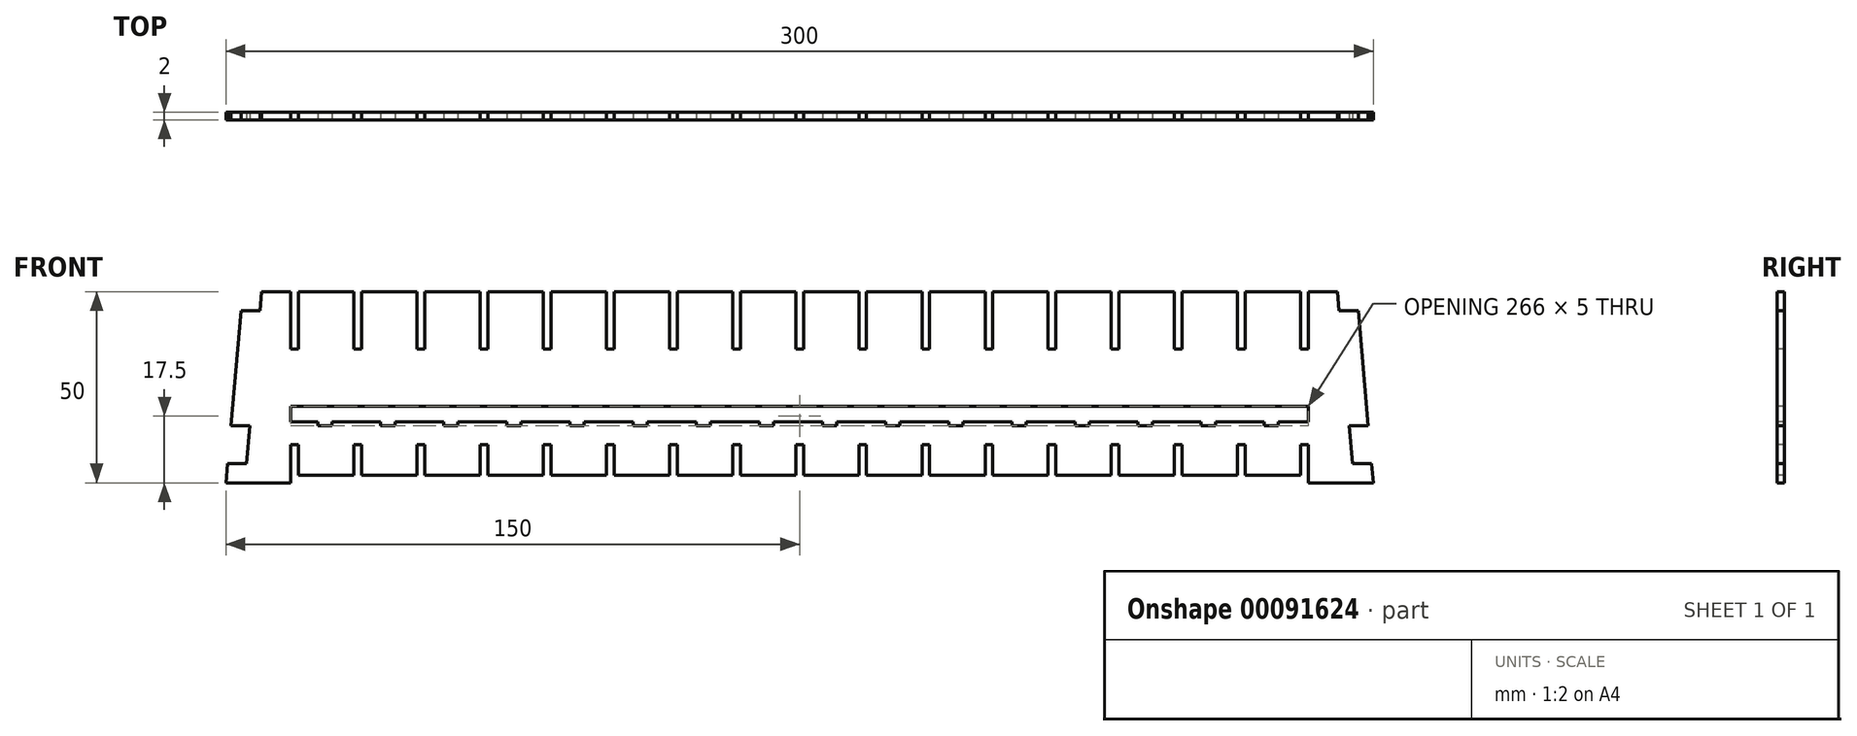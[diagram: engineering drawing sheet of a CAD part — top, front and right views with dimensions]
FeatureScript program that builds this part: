
annotation { "Feature Type Name" : "Feature", "Feature Type Description" : "" }
export const myFeature = defineFeature(function(context is Context, id is Id, definition is map)
    precondition{}
    {
        {
            var Q0;
            Q0=qCreatedBy(makeId("Front.planeOp"),FACE);
            var sketch = newSketch(context, id + "F0", { "sketchPlane" : qUnion([Q0])});
            skLineSegment(sketch, "E0", {"start": v(0, 0) * mm, "end": v(3.94, 45) * mm});
            skLineSegment(sketch, "E1", {"start": v(17, 50) * mm, "end": v(17, 35) * mm});
            skLineSegment(sketch, "E2", {"start": v(17, 35) * mm, "end": v(19, 35) * mm});
            skLineSegment(sketch, "E3", {"start": v(19, 35) * mm, "end": v(19, 50) * mm});
            skLineSegment(sketch, "E4", {"start": v(19, 50) * mm, "end": v(33.5, 50) * mm});
            skLineSegment(sketch, "E5", {"start": v(17, 0) * mm, "end": v(0, 0) * mm});
            skLineSegment(sketch, "E6", {"start": v(33.5, 50) * mm, "end": v(33.5, 35) * mm});
            skLineSegment(sketch, "E7", {"start": v(33.5, 35) * mm, "end": v(35.5, 35) * mm});
            skLineSegment(sketch, "E8", {"start": v(35.5, 35) * mm, "end": v(35.5, 50) * mm});
            skLineSegment(sketch, "E9", {"start": v(35.5, 50) * mm, "end": v(50, 50) * mm});
            skLineSegment(sketch, "E10", {"start": v(50, 50) * mm, "end": v(50, 35) * mm});
            skLineSegment(sketch, "E11", {"start": v(50, 35) * mm, "end": v(52, 35) * mm});
            skLineSegment(sketch, "E12", {"start": v(52, 35) * mm, "end": v(52, 50) * mm});
            skLineSegment(sketch, "E13", {"start": v(52, 50) * mm, "end": v(66.5, 50) * mm});
            skLineSegment(sketch, "E14", {"start": v(66.5, 50) * mm, "end": v(66.5, 35) * mm});
            skLineSegment(sketch, "E15", {"start": v(66.5, 35) * mm, "end": v(68.5, 35) * mm});
            skLineSegment(sketch, "E16", {"start": v(68.5, 35) * mm, "end": v(68.5, 50) * mm});
            skLineSegment(sketch, "E17", {"start": v(68.5, 50) * mm, "end": v(83, 50) * mm});
            skLineSegment(sketch, "E18", {"start": v(83, 50) * mm, "end": v(83, 35) * mm});
            skLineSegment(sketch, "E19", {"start": v(83, 35) * mm, "end": v(85, 35) * mm});
            skLineSegment(sketch, "E20", {"start": v(85, 35) * mm, "end": v(85, 50) * mm});
            skLineSegment(sketch, "E21", {"start": v(85, 50) * mm, "end": v(99.5, 50) * mm});
            skLineSegment(sketch, "E22", {"start": v(99.5, 50) * mm, "end": v(99.5, 35) * mm});
            skLineSegment(sketch, "E23", {"start": v(99.5, 35) * mm, "end": v(101.5, 35) * mm});
            skLineSegment(sketch, "E24", {"start": v(101.5, 35) * mm, "end": v(101.5, 50) * mm});
            skLineSegment(sketch, "E25", {"start": v(101.5, 50) * mm, "end": v(116, 50) * mm});
            skLineSegment(sketch, "E26", {"start": v(116, 50) * mm, "end": v(116, 35) * mm});
            skLineSegment(sketch, "E27", {"start": v(116, 35) * mm, "end": v(118, 35) * mm});
            skLineSegment(sketch, "E28", {"start": v(118, 35) * mm, "end": v(118, 50) * mm});
            skLineSegment(sketch, "E29", {"start": v(118, 50) * mm, "end": v(132.5, 50) * mm});
            skLineSegment(sketch, "E30", {"start": v(132.5, 50) * mm, "end": v(132.5, 35) * mm});
            skLineSegment(sketch, "E31", {"start": v(132.5, 35) * mm, "end": v(134.5, 35) * mm});
            skLineSegment(sketch, "E32", {"start": v(134.5, 35) * mm, "end": v(134.5, 50) * mm});
            skLineSegment(sketch, "E33", {"start": v(134.5, 50) * mm, "end": v(149, 50) * mm});
            skLineSegment(sketch, "E34", {"start": v(149, 50) * mm, "end": v(149, 35) * mm});
            skLineSegment(sketch, "E35", {"start": v(149, 35) * mm, "end": v(151, 35) * mm});
            skLineSegment(sketch, "E36", {"start": v(151, 35) * mm, "end": v(151, 50) * mm});
            skLineSegment(sketch, "E37", {"start": v(151, 50) * mm, "end": v(165.5, 50) * mm});
            skLineSegment(sketch, "E38", {"start": v(165.5, 50) * mm, "end": v(165.5, 35) * mm});
            skLineSegment(sketch, "E39", {"start": v(165.5, 35) * mm, "end": v(167.5, 35) * mm});
            skLineSegment(sketch, "E40", {"start": v(167.5, 35) * mm, "end": v(167.5, 50) * mm});
            skLineSegment(sketch, "E41", {"start": v(167.5, 50) * mm, "end": v(182, 50) * mm});
            skLineSegment(sketch, "E42", {"start": v(182, 50) * mm, "end": v(182, 35) * mm});
            skLineSegment(sketch, "E43", {"start": v(182, 35) * mm, "end": v(184, 35) * mm});
            skLineSegment(sketch, "E44", {"start": v(184, 35) * mm, "end": v(184, 50) * mm});
            skLineSegment(sketch, "E45", {"start": v(184, 50) * mm, "end": v(198.5, 50) * mm});
            skLineSegment(sketch, "E46", {"start": v(198.5, 50) * mm, "end": v(198.5, 35) * mm});
            skLineSegment(sketch, "E47", {"start": v(198.5, 35) * mm, "end": v(200.5, 35) * mm});
            skLineSegment(sketch, "E48", {"start": v(200.5, 35) * mm, "end": v(200.5, 50) * mm});
            skLineSegment(sketch, "E49", {"start": v(200.5, 50) * mm, "end": v(215, 50) * mm});
            skLineSegment(sketch, "E50", {"start": v(215, 50) * mm, "end": v(215, 35) * mm});
            skLineSegment(sketch, "E51", {"start": v(215, 35) * mm, "end": v(217, 35) * mm});
            skLineSegment(sketch, "E52", {"start": v(217, 35) * mm, "end": v(217, 50) * mm});
            skLineSegment(sketch, "E53", {"start": v(217, 50) * mm, "end": v(231.5, 50) * mm});
            skLineSegment(sketch, "E54", {"start": v(231.5, 50) * mm, "end": v(231.5, 35) * mm});
            skLineSegment(sketch, "E55", {"start": v(231.5, 35) * mm, "end": v(233.5, 35) * mm});
            skLineSegment(sketch, "E56", {"start": v(233.5, 35) * mm, "end": v(233.5, 50) * mm});
            skLineSegment(sketch, "E57", {"start": v(233.5, 50) * mm, "end": v(248, 50) * mm});
            skLineSegment(sketch, "E58", {"start": v(248, 50) * mm, "end": v(248, 35) * mm});
            skLineSegment(sketch, "E59", {"start": v(248, 35) * mm, "end": v(250, 35) * mm});
            skLineSegment(sketch, "E60", {"start": v(250, 35) * mm, "end": v(250, 50) * mm});
            skLineSegment(sketch, "E61", {"start": v(250, 50) * mm, "end": v(264.5, 50) * mm});
            skLineSegment(sketch, "E62", {"start": v(264.5, 50) * mm, "end": v(264.5, 35) * mm});
            skLineSegment(sketch, "E63", {"start": v(264.5, 35) * mm, "end": v(266.5, 35) * mm});
            skLineSegment(sketch, "E64", {"start": v(266.5, 35) * mm, "end": v(266.5, 50) * mm});
            skLineSegment(sketch, "E65", {"start": v(300, 0) * mm, "end": v(283, 0) * mm});
            skLineSegment(sketch, "E66", {"start": v(283, 10) * mm, "end": v(281, 10) * mm});
            skLineSegment(sketch, "E67", {"start": v(281, 2) * mm, "end": v(266.5, 2) * mm});
            skLineSegment(sketch, "E68", {"start": v(266.5, 10) * mm, "end": v(264.5, 10) * mm});
            skLineSegment(sketch, "E69", {"start": v(264.5, 2) * mm, "end": v(250, 2) * mm});
            skLineSegment(sketch, "E70", {"start": v(250, 10) * mm, "end": v(248, 10) * mm});
            skLineSegment(sketch, "E71", {"start": v(248, 2) * mm, "end": v(233.5, 2) * mm});
            skLineSegment(sketch, "E72", {"start": v(233.5, 10) * mm, "end": v(231.5, 10) * mm});
            skLineSegment(sketch, "E73", {"start": v(231.5, 2) * mm, "end": v(217, 2) * mm});
            skLineSegment(sketch, "E74", {"start": v(217, 10) * mm, "end": v(215, 10) * mm});
            skLineSegment(sketch, "E75", {"start": v(215, 2) * mm, "end": v(200.5, 2) * mm});
            skLineSegment(sketch, "E76", {"start": v(200.5, 10) * mm, "end": v(198.5, 10) * mm});
            skLineSegment(sketch, "E77", {"start": v(198.5, 2) * mm, "end": v(184, 2) * mm});
            skLineSegment(sketch, "E78", {"start": v(184, 10) * mm, "end": v(182, 10) * mm});
            skLineSegment(sketch, "E79", {"start": v(182, 2) * mm, "end": v(167.5, 2) * mm});
            skLineSegment(sketch, "E80", {"start": v(167.5, 10) * mm, "end": v(165.5, 10) * mm});
            skLineSegment(sketch, "E81", {"start": v(165.5, 2) * mm, "end": v(151, 2) * mm});
            skLineSegment(sketch, "E82", {"start": v(151, 10) * mm, "end": v(149, 10) * mm});
            skLineSegment(sketch, "E83", {"start": v(149, 2) * mm, "end": v(134.5, 2) * mm});
            skLineSegment(sketch, "E84", {"start": v(134.5, 10) * mm, "end": v(132.5, 10) * mm});
            skLineSegment(sketch, "E85", {"start": v(132.5, 2) * mm, "end": v(118, 2) * mm});
            skLineSegment(sketch, "E86", {"start": v(118, 10) * mm, "end": v(116, 10) * mm});
            skLineSegment(sketch, "E87", {"start": v(116, 2) * mm, "end": v(101.5, 2) * mm});
            skLineSegment(sketch, "E88", {"start": v(101.5, 10) * mm, "end": v(99.5, 10) * mm});
            skLineSegment(sketch, "E89", {"start": v(99.5, 2) * mm, "end": v(85, 2) * mm});
            skLineSegment(sketch, "E90", {"start": v(85, 10) * mm, "end": v(83, 10) * mm});
            skLineSegment(sketch, "E91", {"start": v(83, 2) * mm, "end": v(68.5, 2) * mm});
            skLineSegment(sketch, "E92", {"start": v(68.5, 10) * mm, "end": v(66.5, 10) * mm});
            skLineSegment(sketch, "E93", {"start": v(66.5, 2) * mm, "end": v(52, 2) * mm});
            skLineSegment(sketch, "E94", {"start": v(52, 10) * mm, "end": v(50, 10) * mm});
            skLineSegment(sketch, "E95", {"start": v(50, 2) * mm, "end": v(35.5, 2) * mm});
            skLineSegment(sketch, "E96", {"start": v(19, 10) * mm, "end": v(17, 10) * mm});
            skLineSegment(sketch, "E97", {"start": v(19, 10) * mm, "end": v(19, 2) * mm});
            skLineSegment(sketch, "E98", {"start": v(19, 2) * mm, "end": v(33.5, 2) * mm});
            skLineSegment(sketch, "E99", {"start": v(33.5, 2) * mm, "end": v(33.5, 10) * mm});
            skLineSegment(sketch, "E100", {"start": v(33.5, 10) * mm, "end": v(35.5, 10) * mm});
            skLineSegment(sketch, "E101", {"start": v(35.5, 10) * mm, "end": v(35.5, 2) * mm});
            skLineSegment(sketch, "E102", {"start": v(266.5, 50) * mm, "end": v(281, 50) * mm});
            skLineSegment(sketch, "E103", {"start": v(281, 50) * mm, "end": v(281, 35) * mm});
            skLineSegment(sketch, "E104", {"start": v(281, 35) * mm, "end": v(283, 35) * mm});
            skLineSegment(sketch, "E105", {"start": v(283, 35) * mm, "end": v(283, 50) * mm});
            skLineSegment(sketch, "E106", {"start": v(283, 50) * mm, "end": v(290.63, 50) * mm});
            skLineSegment(sketch, "E107", {"start": v(296.06, 45) * mm, "end": v(291.06, 45) * mm});
            skLineSegment(sketch, "E108", {"start": v(291.06, 45) * mm, "end": v(290.63, 50) * mm});
            skLineSegment(sketch, "E109", {"start": v(296.06, 45) * mm, "end": v(300, 0) * mm});
            skLineSegment(sketch, "E110", {"start": v(9.37, 50) * mm, "end": v(8.94, 45) * mm});
            skLineSegment(sketch, "E111", {"start": v(8.94, 45) * mm, "end": v(3.94, 45) * mm});
            skLineSegment(sketch, "E112", {"start": v(9.37, 50) * mm, "end": v(17, 50) * mm});
            skLineSegment(sketch, "E113", {"start": v(17, 0) * mm, "end": v(17, 10) * mm});
            skLineSegment(sketch, "E114", {"start": v(50, 2) * mm, "end": v(50, 10) * mm});
            skLineSegment(sketch, "E115", {"start": v(52, 2) * mm, "end": v(52, 10) * mm});
            skLineSegment(sketch, "E116", {"start": v(66.5, 2) * mm, "end": v(66.5, 10) * mm});
            skLineSegment(sketch, "E117", {"start": v(68.5, 2) * mm, "end": v(68.5, 10) * mm});
            skLineSegment(sketch, "E118", {"start": v(83, 2) * mm, "end": v(83, 10) * mm});
            skLineSegment(sketch, "E119", {"start": v(85, 2) * mm, "end": v(85, 10) * mm});
            skLineSegment(sketch, "E120", {"start": v(99.5, 2) * mm, "end": v(99.5, 10) * mm});
            skLineSegment(sketch, "E121", {"start": v(101.5, 2) * mm, "end": v(101.5, 10) * mm});
            skLineSegment(sketch, "E122", {"start": v(116, 2) * mm, "end": v(116, 10) * mm});
            skLineSegment(sketch, "E123", {"start": v(118, 2) * mm, "end": v(118, 10) * mm});
            skLineSegment(sketch, "E124", {"start": v(132.5, 2) * mm, "end": v(132.5, 10) * mm});
            skLineSegment(sketch, "E125", {"start": v(134.5, 2) * mm, "end": v(134.5, 10) * mm});
            skLineSegment(sketch, "E126", {"start": v(149, 2) * mm, "end": v(149, 10) * mm});
            skLineSegment(sketch, "E127", {"start": v(151, 2) * mm, "end": v(151, 10) * mm});
            skLineSegment(sketch, "E128", {"start": v(165.5, 2) * mm, "end": v(165.5, 10) * mm});
            skLineSegment(sketch, "E129", {"start": v(167.5, 2) * mm, "end": v(167.5, 10) * mm});
            skLineSegment(sketch, "E130", {"start": v(182, 2) * mm, "end": v(182, 10) * mm});
            skLineSegment(sketch, "E131", {"start": v(184, 2) * mm, "end": v(184, 10) * mm});
            skLineSegment(sketch, "E132", {"start": v(198.5, 2) * mm, "end": v(198.5, 10) * mm});
            skLineSegment(sketch, "E133", {"start": v(200.5, 2) * mm, "end": v(200.5, 10) * mm});
            skLineSegment(sketch, "E134", {"start": v(215, 2) * mm, "end": v(215, 10) * mm});
            skLineSegment(sketch, "E135", {"start": v(217, 2) * mm, "end": v(217, 10) * mm});
            skLineSegment(sketch, "E136", {"start": v(231.5, 2) * mm, "end": v(231.5, 10) * mm});
            skLineSegment(sketch, "E137", {"start": v(233.5, 2) * mm, "end": v(233.5, 10) * mm});
            skLineSegment(sketch, "E138", {"start": v(248, 2) * mm, "end": v(248, 10) * mm});
            skLineSegment(sketch, "E139", {"start": v(250, 2) * mm, "end": v(250, 10) * mm});
            skLineSegment(sketch, "E140", {"start": v(264.5, 2) * mm, "end": v(264.5, 10) * mm});
            skLineSegment(sketch, "E141", {"start": v(266.5, 2) * mm, "end": v(266.5, 10) * mm});
            skLineSegment(sketch, "E142", {"start": v(281, 2) * mm, "end": v(281, 10) * mm});
            skLineSegment(sketch, "E143", {"start": v(283, 0) * mm, "end": v(283, 10) * mm});
            skSolve(sketch);
        }
        {
            var Q0;
            Q0=makeQuery(id+"F0.imprint","IMPRINT",FACE,{"disambiguationData":[TD([[makeQuery(id+"F0.imprint","IMPRINT",EDGE,{"derivedFrom":sQuery(id+"F0.wireOp",EDGE,"E0")}),-1.0]])]});
            extrude(context, id + "F1", {"entities" : qUnion([Q0]), "oppositeDirection" : true, "depth" : 2 * mm});
        }
        {
            var Q0;
            Q0=qCreatedBy(makeId("Front.planeOp"),FACE);
            var sketch = newSketch(context, id + "F2", { "sketchPlane" : qUnion([Q0])});
            skLineSegment(sketch, "E144", {"start": v(17, 20) * mm, "end": v(283, 20) * mm});
            skLineSegment(sketch, "E145", {"start": v(283, 20) * mm, "end": v(283, 16) * mm});
            skLineSegment(sketch, "E146", {"start": v(17, 20) * mm, "end": v(17, 16) * mm});
            skLineSegment(sketch, "E147", {"start": v(17, 16) * mm, "end": v(24, 16) * mm});
            skLineSegment(sketch, "E148", {"start": v(24, 16) * mm, "end": v(24, 15) * mm});
            skLineSegment(sketch, "E149", {"start": v(24, 15) * mm, "end": v(27.7, 15) * mm});
            skLineSegment(sketch, "E150", {"start": v(27.7, 15) * mm, "end": v(27.7, 16) * mm});
            skLineSegment(sketch, "E151", {"start": v(27.7, 16) * mm, "end": v(40.5, 16) * mm});
            skLineSegment(sketch, "E152", {"start": v(40.5, 16) * mm, "end": v(40.5, 15) * mm});
            skLineSegment(sketch, "E153", {"start": v(40.5, 15) * mm, "end": v(44.2, 15) * mm});
            skLineSegment(sketch, "E154", {"start": v(44.2, 15) * mm, "end": v(44.2, 16) * mm});
            skLineSegment(sketch, "E155", {"start": v(44.2, 16) * mm, "end": v(57, 16) * mm});
            skLineSegment(sketch, "E156", {"start": v(57, 16) * mm, "end": v(57, 15) * mm});
            skLineSegment(sketch, "E157", {"start": v(57, 15) * mm, "end": v(60.7, 15) * mm});
            skLineSegment(sketch, "E158", {"start": v(60.7, 15) * mm, "end": v(60.7, 16) * mm});
            skLineSegment(sketch, "E159", {"start": v(60.7, 16) * mm, "end": v(73.5, 16) * mm});
            skLineSegment(sketch, "E160", {"start": v(73.5, 16) * mm, "end": v(73.5, 15) * mm});
            skLineSegment(sketch, "E161", {"start": v(93.7, 16) * mm, "end": v(93.7, 15) * mm});
            skLineSegment(sketch, "E162", {"start": v(93.7, 15) * mm, "end": v(90, 15) * mm});
            skLineSegment(sketch, "E163", {"start": v(90, 15) * mm, "end": v(90, 16) * mm});
            skLineSegment(sketch, "E164", {"start": v(106.5, 16) * mm, "end": v(106.5, 15) * mm});
            skLineSegment(sketch, "E165", {"start": v(106.5, 15) * mm, "end": v(110.2, 15) * mm});
            skLineSegment(sketch, "E166", {"start": v(110.2, 15) * mm, "end": v(110.2, 16) * mm});
            skLineSegment(sketch, "E167", {"start": v(110.2, 16) * mm, "end": v(123, 16) * mm});
            skLineSegment(sketch, "E168", {"start": v(123, 16) * mm, "end": v(123, 15) * mm});
            skLineSegment(sketch, "E169", {"start": v(123, 15) * mm, "end": v(126.7, 15) * mm});
            skLineSegment(sketch, "E170", {"start": v(126.7, 15) * mm, "end": v(126.7, 16) * mm});
            skLineSegment(sketch, "E171", {"start": v(126.7, 16) * mm, "end": v(139.5, 16) * mm});
            skLineSegment(sketch, "E172", {"start": v(139.5, 16) * mm, "end": v(139.5, 15) * mm});
            skLineSegment(sketch, "E173", {"start": v(139.5, 15) * mm, "end": v(143.2, 15) * mm});
            skLineSegment(sketch, "E174", {"start": v(143.2, 15) * mm, "end": v(143.2, 16) * mm});
            skLineSegment(sketch, "E175", {"start": v(143.2, 16) * mm, "end": v(156, 16) * mm});
            skLineSegment(sketch, "E176", {"start": v(156, 16) * mm, "end": v(156, 15) * mm});
            skLineSegment(sketch, "E177", {"start": v(156, 15) * mm, "end": v(159.7, 15) * mm});
            skLineSegment(sketch, "E178", {"start": v(159.7, 15) * mm, "end": v(159.7, 16) * mm});
            skLineSegment(sketch, "E179", {"start": v(159.7, 16) * mm, "end": v(172.5, 16) * mm});
            skLineSegment(sketch, "E180", {"start": v(172.5, 16) * mm, "end": v(172.5, 15) * mm});
            skLineSegment(sketch, "E181", {"start": v(172.5, 15) * mm, "end": v(176.2, 15) * mm});
            skLineSegment(sketch, "E182", {"start": v(176.2, 15) * mm, "end": v(176.2, 16) * mm});
            skLineSegment(sketch, "E183", {"start": v(238.5, 16) * mm, "end": v(238.5, 15) * mm});
            skLineSegment(sketch, "E184", {"start": v(238.5, 15) * mm, "end": v(242.2, 15) * mm});
            skLineSegment(sketch, "E185", {"start": v(242.2, 15) * mm, "end": v(242.2, 16) * mm});
            skLineSegment(sketch, "E186", {"start": v(242.2, 16) * mm, "end": v(255, 16) * mm});
            skLineSegment(sketch, "E187", {"start": v(255, 16) * mm, "end": v(255, 15) * mm});
            skLineSegment(sketch, "E188", {"start": v(255, 15) * mm, "end": v(258.7, 15) * mm});
            skLineSegment(sketch, "E189", {"start": v(258.7, 15) * mm, "end": v(258.7, 16) * mm});
            skLineSegment(sketch, "E190", {"start": v(258.7, 16) * mm, "end": v(271.5, 16) * mm});
            skLineSegment(sketch, "E191", {"start": v(271.5, 16) * mm, "end": v(271.5, 15) * mm});
            skLineSegment(sketch, "E192", {"start": v(271.5, 15) * mm, "end": v(275.2, 15) * mm});
            skLineSegment(sketch, "E193", {"start": v(275.2, 15) * mm, "end": v(275.2, 16) * mm});
            skLineSegment(sketch, "E194", {"start": v(189, 16) * mm, "end": v(189, 15) * mm});
            skLineSegment(sketch, "E195", {"start": v(189, 15) * mm, "end": v(192.7, 15) * mm});
            skLineSegment(sketch, "E196", {"start": v(192.7, 15) * mm, "end": v(192.7, 16) * mm});
            skLineSegment(sketch, "E197", {"start": v(192.7, 16) * mm, "end": v(205.5, 16) * mm});
            skLineSegment(sketch, "E198", {"start": v(205.5, 16) * mm, "end": v(205.5, 15) * mm});
            skLineSegment(sketch, "E199", {"start": v(205.5, 15) * mm, "end": v(209.2, 15) * mm});
            skLineSegment(sketch, "E200", {"start": v(209.2, 15) * mm, "end": v(209.2, 16) * mm});
            skLineSegment(sketch, "E201", {"start": v(209.2, 16) * mm, "end": v(222, 16) * mm});
            skLineSegment(sketch, "E202", {"start": v(222, 16) * mm, "end": v(222, 15) * mm});
            skLineSegment(sketch, "E203", {"start": v(222, 15) * mm, "end": v(225.7, 15) * mm});
            skLineSegment(sketch, "E204", {"start": v(225.7, 15) * mm, "end": v(225.7, 16) * mm});
            skLineSegment(sketch, "E205", {"start": v(73.5, 15) * mm, "end": v(77.2, 15) * mm});
            skLineSegment(sketch, "E206", {"start": v(77.2, 15) * mm, "end": v(77.2, 16) * mm});
            skLineSegment(sketch, "E207", {"start": v(77.2, 16) * mm, "end": v(90, 16) * mm});
            skLineSegment(sketch, "E208", {"start": v(93.7, 16) * mm, "end": v(106.5, 16) * mm});
            skLineSegment(sketch, "E209", {"start": v(176.2, 16) * mm, "end": v(189, 16) * mm});
            skLineSegment(sketch, "E210", {"start": v(225.7, 16) * mm, "end": v(238.5, 16) * mm});
            skLineSegment(sketch, "E211", {"start": v(275.2, 16) * mm, "end": v(283, 16) * mm});
            skLineSegment(sketch, "E212", {"start": v(0.44, 5) * mm, "end": v(5.44, 5) * mm});
            skLineSegment(sketch, "E213", {"start": v(5.44, 5) * mm, "end": v(6.31, 15) * mm});
            skLineSegment(sketch, "E214", {"start": v(6.31, 15) * mm, "end": v(1.31, 15) * mm});
            skLineSegment(sketch, "E215", {"start": v(1.31, 15) * mm, "end": v(0.44, 5) * mm});
            skLineSegment(sketch, "E216", {"start": v(293.69, 15) * mm, "end": v(294.56, 5) * mm});
            skLineSegment(sketch, "E217", {"start": v(294.56, 5) * mm, "end": v(299.56, 5) * mm});
            skLineSegment(sketch, "E218", {"start": v(299.56, 5) * mm, "end": v(298.69, 15) * mm});
            skLineSegment(sketch, "E219", {"start": v(298.69, 15) * mm, "end": v(293.69, 15) * mm});
            skSolve(sketch);
        }
        {
            var Q0;
            Q0 = qSketchRegion(id + "F2", true);
            var Q1;
            Q1=makeQuery(id+"F1.opExtrude","CAP_FACE",FACE,{"disambiguationData":[OSD([sQuery(id+"F0.wireOp",EDGE,"E0"),sQuery(id+"F0.wireOp",EDGE,"HgcZy7nT-3lwv-bNy9-udKW-1yyANhBGPKqc"),sQuery(id+"F0.wireOp",EDGE,"E1"),sQuery(id+"F0.wireOp",EDGE,"E2"),sQuery(id+"F0.wireOp",EDGE,"E3"),sQuery(id+"F0.wireOp",EDGE,"E4"),sQuery(id+"F0.wireOp",EDGE,"E5"),sQuery(id+"F0.wireOp",EDGE,"E6"),sQuery(id+"F0.wireOp",EDGE,"E7"),sQuery(id+"F0.wireOp",EDGE,"E8"),sQuery(id+"F0.wireOp",EDGE,"E9"),sQuery(id+"F0.wireOp",EDGE,"E10"),sQuery(id+"F0.wireOp",EDGE,"E11"),sQuery(id+"F0.wireOp",EDGE,"E12"),sQuery(id+"F0.wireOp",EDGE,"E13"),sQuery(id+"F0.wireOp",EDGE,"E14"),sQuery(id+"F0.wireOp",EDGE,"E15"),sQuery(id+"F0.wireOp",EDGE,"E16"),sQuery(id+"F0.wireOp",EDGE,"E17"),sQuery(id+"F0.wireOp",EDGE,"E18"),sQuery(id+"F0.wireOp",EDGE,"E19"),sQuery(id+"F0.wireOp",EDGE,"E20"),sQuery(id+"F0.wireOp",EDGE,"E21"),sQuery(id+"F0.wireOp",EDGE,"E22"),sQuery(id+"F0.wireOp",EDGE,"E23"),sQuery(id+"F0.wireOp",EDGE,"E24"),sQuery(id+"F0.wireOp",EDGE,"E25"),sQuery(id+"F0.wireOp",EDGE,"E26"),sQuery(id+"F0.wireOp",EDGE,"E27"),sQuery(id+"F0.wireOp",EDGE,"E28"),sQuery(id+"F0.wireOp",EDGE,"E29"),sQuery(id+"F0.wireOp",EDGE,"E30"),sQuery(id+"F0.wireOp",EDGE,"E31"),sQuery(id+"F0.wireOp",EDGE,"E32"),sQuery(id+"F0.wireOp",EDGE,"E33"),sQuery(id+"F0.wireOp",EDGE,"E34"),sQuery(id+"F0.wireOp",EDGE,"E35"),sQuery(id+"F0.wireOp",EDGE,"E36"),sQuery(id+"F0.wireOp",EDGE,"E37"),sQuery(id+"F0.wireOp",EDGE,"E38"),sQuery(id+"F0.wireOp",EDGE,"E39"),sQuery(id+"F0.wireOp",EDGE,"E40"),sQuery(id+"F0.wireOp",EDGE,"E41"),sQuery(id+"F0.wireOp",EDGE,"E42"),sQuery(id+"F0.wireOp",EDGE,"E43"),sQuery(id+"F0.wireOp",EDGE,"E44"),sQuery(id+"F0.wireOp",EDGE,"E45"),sQuery(id+"F0.wireOp",EDGE,"E46"),sQuery(id+"F0.wireOp",EDGE,"E47"),sQuery(id+"F0.wireOp",EDGE,"E48"),sQuery(id+"F0.wireOp",EDGE,"E49"),sQuery(id+"F0.wireOp",EDGE,"E50"),sQuery(id+"F0.wireOp",EDGE,"E51"),sQuery(id+"F0.wireOp",EDGE,"E52"),sQuery(id+"F0.wireOp",EDGE,"E53"),sQuery(id+"F0.wireOp",EDGE,"E54"),sQuery(id+"F0.wireOp",EDGE,"E55"),sQuery(id+"F0.wireOp",EDGE,"E56"),sQuery(id+"F0.wireOp",EDGE,"E57"),sQuery(id+"F0.wireOp",EDGE,"E58"),sQuery(id+"F0.wireOp",EDGE,"E59"),sQuery(id+"F0.wireOp",EDGE,"E60"),sQuery(id+"F0.wireOp",EDGE,"E61"),sQuery(id+"F0.wireOp",EDGE,"E62"),sQuery(id+"F0.wireOp",EDGE,"E63"),sQuery(id+"F0.wireOp",EDGE,"E64"),sQuery(id+"F0.wireOp",EDGE,"BVOWMFHa-wpLm-4TX3-Hbss-mqhhteEW6FXH"),sQuery(id+"F0.wireOp",EDGE,"E65"),sQuery(id+"F0.wireOp",EDGE,"Ny0LBNpl-DC1b-g7gX-uDmU-KXUJp1Uvs8bH"),sQuery(id+"F0.wireOp",EDGE,"E66"),sQuery(id+"F0.wireOp",EDGE,"L0EVueSU-Bzzz-ozeF-6hyl-cjv2B7mdk9nX"),sQuery(id+"F0.wireOp",EDGE,"E67"),sQuery(id+"F0.wireOp",EDGE,"z7V8Xtq7-9ljz-YrJZ-rfjC-Y5BD1rRiIm1u"),sQuery(id+"F0.wireOp",EDGE,"E68"),sQuery(id+"F0.wireOp",EDGE,"YCztE2ad-vpCO-r5Er-xRay-cPCHDfHWENhY"),sQuery(id+"F0.wireOp",EDGE,"E69"),sQuery(id+"F0.wireOp",EDGE,"hall3pES-sXyJ-vu0Y-LRwG-adX0xoJdBjPT"),sQuery(id+"F0.wireOp",EDGE,"E70"),sQuery(id+"F0.wireOp",EDGE,"HapMSiuU-j1My-omjA-AIKl-s35L9K1DCdMv"),sQuery(id+"F0.wireOp",EDGE,"E71"),sQuery(id+"F0.wireOp",EDGE,"cxGI27vh-PhuA-DEnV-wgYv-RIFEEykBdlIG"),sQuery(id+"F0.wireOp",EDGE,"E72"),sQuery(id+"F0.wireOp",EDGE,"4pOcXCnN-Qqmk-RNP6-p9ZY-k7VT3SrKYYIm"),sQuery(id+"F0.wireOp",EDGE,"E73"),sQuery(id+"F0.wireOp",EDGE,"IvOV3hIr-bj6g-dsOc-59va-o6hrhdawShYW"),sQuery(id+"F0.wireOp",EDGE,"E74"),sQuery(id+"F0.wireOp",EDGE,"aiYAQkSz-ye5B-NAvN-EaHV-yYgKXb2guKy2"),sQuery(id+"F0.wireOp",EDGE,"E75"),sQuery(id+"F0.wireOp",EDGE,"deSUF8Wy-izGZ-KJL7-F7sa-vv7DJSF65tzd"),sQuery(id+"F0.wireOp",EDGE,"E76"),sQuery(id+"F0.wireOp",EDGE,"knURT3mm-qJ5e-uAEv-XtMx-gx8QacUYlODw"),sQuery(id+"F0.wireOp",EDGE,"E77"),sQuery(id+"F0.wireOp",EDGE,"JvS8wIF9-GTxq-Shxd-HEk2-VQDqqqWf2vDR"),sQuery(id+"F0.wireOp",EDGE,"E78"),sQuery(id+"F0.wireOp",EDGE,"hC3mFLkM-rNt6-YxLP-T6Ut-VB35484fw7rg"),sQuery(id+"F0.wireOp",EDGE,"E79"),sQuery(id+"F0.wireOp",EDGE,"03HSr1IS-cMoz-EuO1-jhf5-BLUVcBS5aCII"),sQuery(id+"F0.wireOp",EDGE,"E80"),sQuery(id+"F0.wireOp",EDGE,"4pRiP4Qb-GxdF-G7ua-kPKT-rGo3PBmFVMMh"),sQuery(id+"F0.wireOp",EDGE,"E81"),sQuery(id+"F0.wireOp",EDGE,"31KDk3w8-zvsP-PMm4-8rSG-4di7emiA55pW"),sQuery(id+"F0.wireOp",EDGE,"E82"),sQuery(id+"F0.wireOp",EDGE,"8IrskNiL-fo41-gDwx-3q5M-fVGG1YOBFxI9"),sQuery(id+"F0.wireOp",EDGE,"E83"),sQuery(id+"F0.wireOp",EDGE,"CSi5XsMw-pvjV-rWde-ON5c-3UqJn2YIq8jn"),sQuery(id+"F0.wireOp",EDGE,"E84"),sQuery(id+"F0.wireOp",EDGE,"MBxpImWm-eRvk-aWU8-U4yn-nKg3TTCsLjfT"),sQuery(id+"F0.wireOp",EDGE,"E85"),sQuery(id+"F0.wireOp",EDGE,"FSR2KC9K-EGrI-nhKE-Fi6A-T41pzSywKCEg"),sQuery(id+"F0.wireOp",EDGE,"E86"),sQuery(id+"F0.wireOp",EDGE,"I2Vx5CsF-7VTe-yqni-W39r-mekiYP3QSefZ"),sQuery(id+"F0.wireOp",EDGE,"E87"),sQuery(id+"F0.wireOp",EDGE,"0cDBUIyj-6oQs-NqVM-rf7f-aOtaGS2aotWP"),sQuery(id+"F0.wireOp",EDGE,"E88"),sQuery(id+"F0.wireOp",EDGE,"yMGYaIAU-y6q6-IKF7-ToxC-SvuajWYre8og"),sQuery(id+"F0.wireOp",EDGE,"E89"),sQuery(id+"F0.wireOp",EDGE,"ZftYtxsV-UZJY-z8ZW-g9Gq-ohFEgne7n6v0"),sQuery(id+"F0.wireOp",EDGE,"E90"),sQuery(id+"F0.wireOp",EDGE,"vxcZILMP-886a-ghS7-RbWO-ZaSI4S1PIg1K"),sQuery(id+"F0.wireOp",EDGE,"E91"),sQuery(id+"F0.wireOp",EDGE,"IlgRW5Ga-Fsin-zCQm-a4KG-mxPj2x5quiJ4"),sQuery(id+"F0.wireOp",EDGE,"E92"),sQuery(id+"F0.wireOp",EDGE,"zQP4WX22-XsxW-SWvl-jWig-XTAqm5llDSmK"),sQuery(id+"F0.wireOp",EDGE,"E93"),sQuery(id+"F0.wireOp",EDGE,"OQ0uxrJ9-YOf8-i4xL-ogb8-zCvbwl5xDN57"),sQuery(id+"F0.wireOp",EDGE,"E94"),sQuery(id+"F0.wireOp",EDGE,"JCZAKs25-YOuf-8OKZ-4fvG-gDuP2TVhTKYT"),sQuery(id+"F0.wireOp",EDGE,"E95"),sQuery(id+"F0.wireOp",EDGE,"E96"),sQuery(id+"F0.wireOp",EDGE,"P1PESZwT-Sg2v-Tdse-M8t0-1K99oKy4DD9l"),sQuery(id+"F0.wireOp",EDGE,"E97"),sQuery(id+"F0.wireOp",EDGE,"E98"),sQuery(id+"F0.wireOp",EDGE,"E99"),sQuery(id+"F0.wireOp",EDGE,"E100"),sQuery(id+"F0.wireOp",EDGE,"E101"),sQuery(id+"F0.wireOp",EDGE,"E102"),sQuery(id+"F0.wireOp",EDGE,"E103"),sQuery(id+"F0.wireOp",EDGE,"E104"),sQuery(id+"F0.wireOp",EDGE,"E105"),sQuery(id+"F0.wireOp",EDGE,"E106")])],"isStart":false});
            extrude(context, id + "F3", {"entities" : qUnion([Q0]), "operationType" : NewBodyOperationType.REMOVE, "endBound" : BoundingType.UP_TO_SURFACE, "oppositeDirection" : true, "endBoundEntityFace" : qUnion([Q1]), "depth" : 25 * mm});
        }
    });
